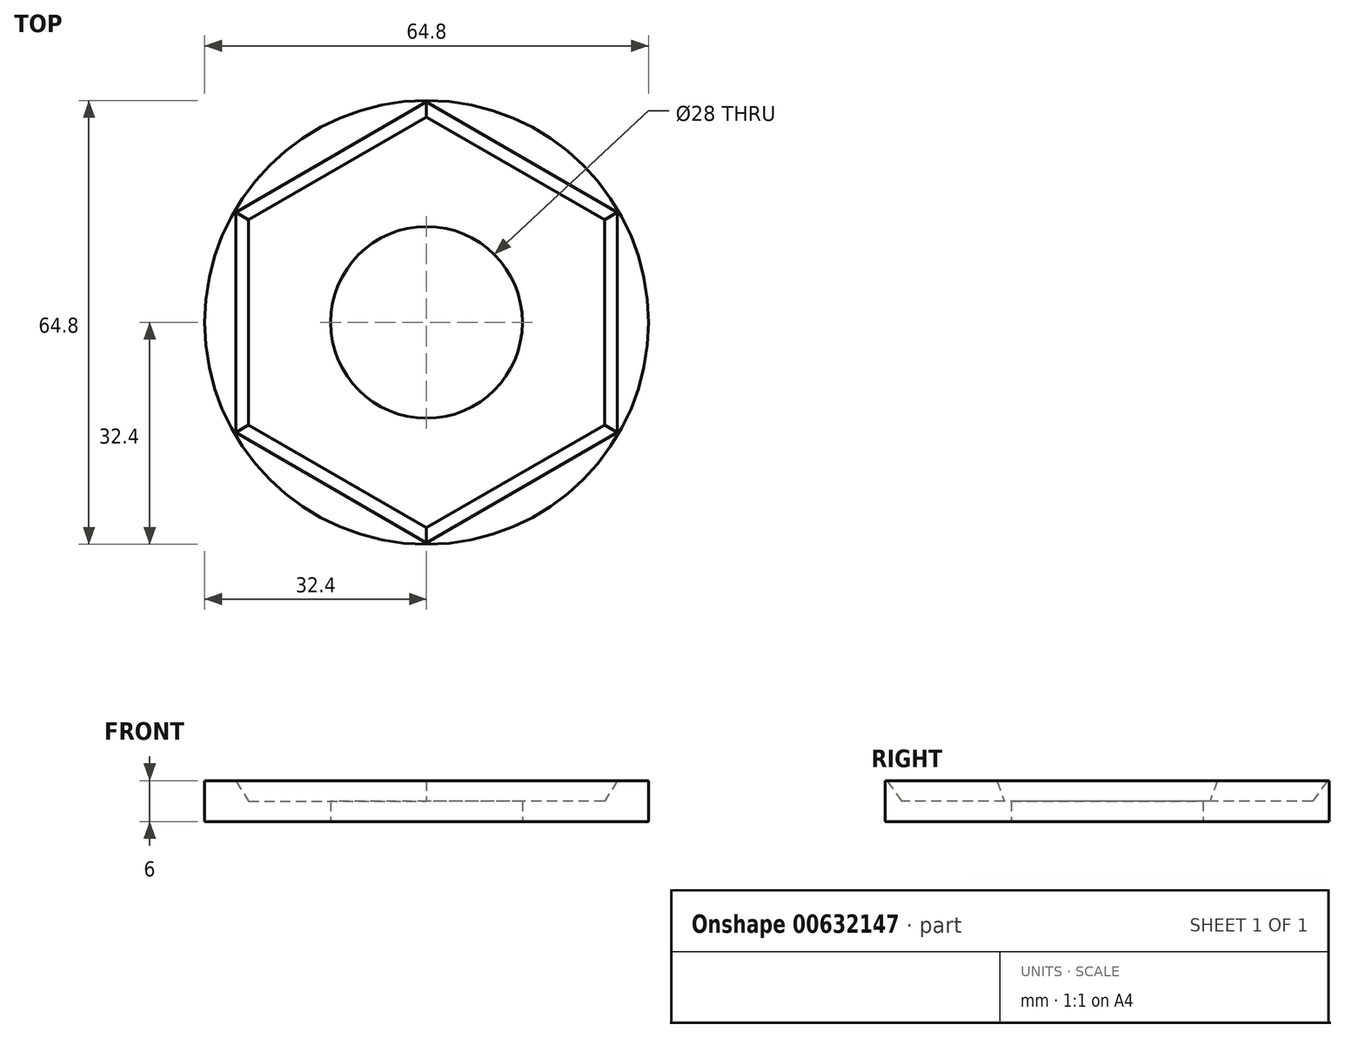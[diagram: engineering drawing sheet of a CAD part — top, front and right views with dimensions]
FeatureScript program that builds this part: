
annotation { "Feature Type Name" : "Feature", "Feature Type Description" : "" }
export const myFeature = defineFeature(function(context is Context, id is Id, definition is map)
    precondition{}
    {
        {
            var Q0;
            Q0=qCreatedBy(makeId("Top.planeOp"),FACE);
            var sketch = newSketch(context, id + "F0", { "sketchPlane" : qUnion([Q0])});
            skCircle(sketch, "E0", {"center": v(0, 0) * mm, "radius": 14 * mm});
            skCircle(sketch, "E1", {"center": v(0, 0) * mm, "radius": 30 * mm});
            skCircle(sketch, "E2.cCircle", {"center": v(0, 0) * mm, "radius": 30 * mm, "construction": true});
            skLineSegment(sketch, "E2.0", {"start": v(25.98, -15) * mm, "end": v(0, -30) * mm});
            skLineSegment(sketch, "E2.1", {"start": v(0, -30) * mm, "end": v(-25.98, -15) * mm});
            skLineSegment(sketch, "E2.2", {"start": v(-25.98, -15) * mm, "end": v(-25.98, 15) * mm});
            skLineSegment(sketch, "E2.3", {"start": v(-25.98, 15) * mm, "end": v(0, 30) * mm});
            skLineSegment(sketch, "E2.4", {"start": v(0, 30) * mm, "end": v(25.98, 15) * mm});
            skLineSegment(sketch, "E2.5", {"start": v(25.98, 15) * mm, "end": v(25.98, -15) * mm});
            skCircle(sketch, "E3.0", {"center": v(0, 0) * mm, "radius": 32.4 * mm});
            skSolve(sketch);
        }
        {
            var Q0;
            {var subQ0=sQuery(id+"F0.wireOp",EDGE,"E2.0");Q0=makeQuery(id+"F0.imprint","IMPRINT",FACE,{"disambiguationData":[TD([[makeQuery(id+"F0.imprint","IMPRINT",EDGE,{"derivedFrom":subQ0}),1.0]])]});}
            var Q1;
            {var subQ0=sQuery(id+"F0.wireOp",EDGE,"E2.5");Q1=makeQuery(id+"F0.imprint","IMPRINT",FACE,{"disambiguationData":[TD([[makeQuery(id+"F0.imprint","IMPRINT",EDGE,{"derivedFrom":subQ0}),1.0]])]});}
            var Q2;
            {var subQ0=sQuery(id+"F0.wireOp",EDGE,"E2.4");Q2=makeQuery(id+"F0.imprint","IMPRINT",FACE,{"disambiguationData":[TD([[makeQuery(id+"F0.imprint","IMPRINT",EDGE,{"derivedFrom":subQ0}),1.0]])]});}
            var Q3;
            {var subQ0=sQuery(id+"F0.wireOp",EDGE,"E2.3");Q3=makeQuery(id+"F0.imprint","IMPRINT",FACE,{"disambiguationData":[TD([[makeQuery(id+"F0.imprint","IMPRINT",EDGE,{"derivedFrom":subQ0}),1.0]])]});}
            var Q4;
            {var subQ0=sQuery(id+"F0.wireOp",EDGE,"E2.2");Q4=makeQuery(id+"F0.imprint","IMPRINT",FACE,{"disambiguationData":[TD([[makeQuery(id+"F0.imprint","IMPRINT",EDGE,{"derivedFrom":subQ0}),1.0]])]});}
            var Q5;
            {var subQ0=sQuery(id+"F0.wireOp",EDGE,"E2.1");Q5=makeQuery(id+"F0.imprint","IMPRINT",FACE,{"disambiguationData":[TD([[makeQuery(id+"F0.imprint","IMPRINT",EDGE,{"derivedFrom":subQ0}),1.0]])]});}
            var Q6;
            Q6=makeQuery(id+"F0.imprint","IMPRINT",FACE,{"disambiguationData":[TD([[makeQuery(id+"F0.imprint","IMPRINT",EDGE,{"derivedFrom":sQuery(id+"F0.wireOp",EDGE,"E3.0")}),1.0]])]});
            extrude(context, id + "F1", {"entities" : qUnion([Q0, Q1, Q2, Q3, Q4, Q5, Q6]), "depth" : 6 * mm, "offsetDistance" : 25 * mm});
        }
        {
            var Q0;
            Q0=makeQuery(id+"F0.imprint","IMPRINT",FACE,{"disambiguationData":[TD([[makeQuery(id+"F0.imprint","IMPRINT",EDGE,{"derivedFrom":sQuery(id+"F0.wireOp",EDGE,"E0")}),-1.0]])]});
            extrude(context, id + "F2", {"entities" : qUnion([Q0]), "operationType" : NewBodyOperationType.ADD, "depth" : 3 * mm, "offsetDistance" : 25 * mm});
        }
        {
            var Q0;
            Q0=makeQuery(id+"F2.opExtrude","CAP_FACE",FACE,{"disambiguationData":[OSD([sQuery(id+"F0.wireOp",EDGE,"E0"),sQuery(id+"F0.wireOp",EDGE,"E2.0"),sQuery(id+"F0.wireOp",EDGE,"E2.1"),sQuery(id+"F0.wireOp",EDGE,"E2.2"),sQuery(id+"F0.wireOp",EDGE,"E2.3"),sQuery(id+"F0.wireOp",EDGE,"E2.4"),sQuery(id+"F0.wireOp",EDGE,"E2.5")])],"isStart":false});
            extrude(context, id + "F3", {"entities" : qUnion([Q0]), "operationType" : NewBodyOperationType.REMOVE, "depth" : 25 * mm, "offsetDistance" : 25 * mm, "hasDraft" : true, "draftAngle" : 32 * degree});
        }
    });
